# Revit family: PRD_FrankeWS_HygieneBagDispenser_HBD191
name_source: partatom
category: Furniture
revit_build: Autodesk Revit 2018 (Build: 20190510_1515(x64)
units: mm (PartAtom-declared; Revit-internal decimal feet)

## family parameters
Cut with Voids When Loaded = No
Host = Face
OmniClass Number = 23.40.20.21
OmniClass Title = Toilet and Bath Specialties
Room Calculation Point = No
Shared = No

## types (1)
- HBD191
    AssetType = Fixed
    BIMObjectName = PRD_AR_HygieneBagDispenser_HBD191
    Category = Pr_40_70_22, Dispensers and acceptance units
    Color = Stainless steel
    Default Elevation = 650 mm  [stored 2.13255 ft]
    Description = Hygiene bag dispenser for wall mounting, stainless steel, surface satin finished with InoxPlus surface refinement for the reduction of finger marks and better cleaning characteristic (easy to clean), material thickness 1.2 mm, edges not welded, inboard lug to hold package, withdrawal from front, incl. premounted double side self-adhesive tap and stainless steel screws and dowels, incl. acetone rag to clean bonding surface.
    DispenserMaterial = PRD_AR_StainlessSteel_SatinFinished
    DurationUnit = year
    Features = stainless steel, 1.20 mm, satin finished, wall mounting, 92x150x22 mm (WxHxD)
    FillingQuantity = 30 Pieces
    Finish = Satin finished
    GrossWeight = 0.30 kg
    IfcExportAs = IfcFurnitureType
    IfcExportType = NOTDEFINED
    MainColor = Stainless steel
    Manufacturer = KWC Group AG
    ManufacturerName = KWC Group AG
    ManufacturerURL = www.kwc.com
    Material = Stainless steel
    Model = HBD191
    ModelNumber = 2000057080
    ModelReference = HBD191
    Name = Hygiene bag dispenser HBD191
    NetWeight = 0.24 kg
    NominalDepth = 22 mm  [stored 0.0721785 ft]
    NominalHeight = 150 mm  [stored 0.492126 ft]
    NominalLength = 92 mm  [stored 0.301837 ft]
    NominalWidth = 92 mm  [stored 0.301837 ft]
    ProductInformation = https://pim.kwc.com
    Size = 92x150x22 mm
    Style = Hygiene bag dispenser
    SurfaceTreatment = InoxPlus (anti fingerprint)
    URL = www.kwc.com
    Version = 1
    WarrantyDurationUnit = year

note: [stored X ft] marks values corroborated as IEEE doubles in the binary element streams (Revit-internal decimal feet)

## geometry (parser evidence)
native form markers: Sweep x2
no freeform markers — native parametric forms only
